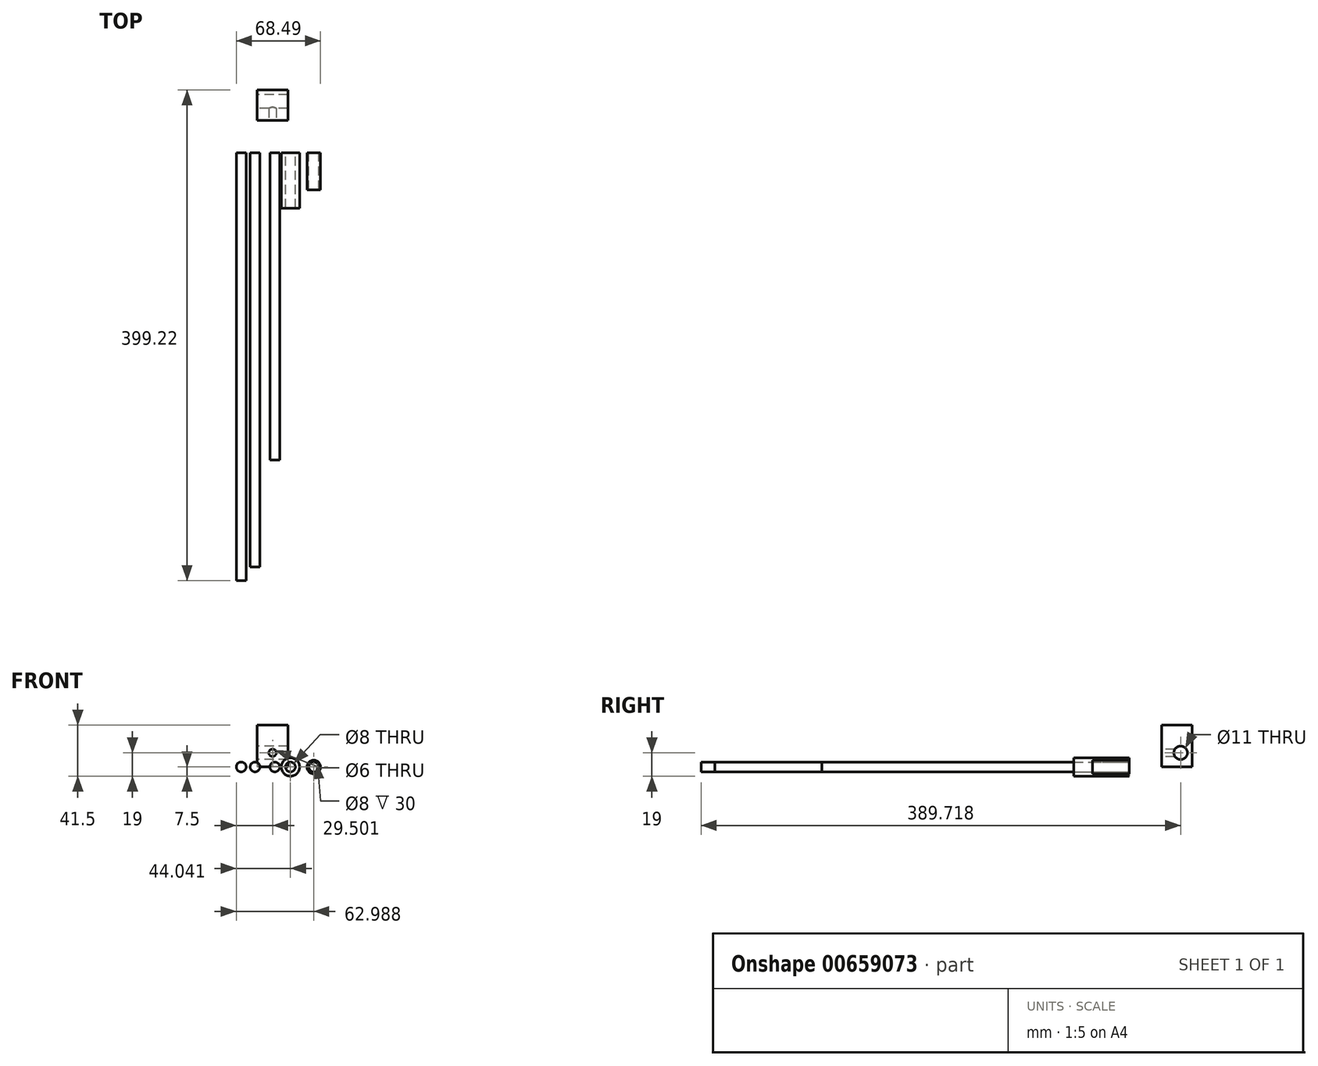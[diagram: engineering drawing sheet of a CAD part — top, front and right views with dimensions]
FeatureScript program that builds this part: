
annotation { "Feature Type Name" : "Feature", "Feature Type Description" : "" }
export const myFeature = defineFeature(function(context is Context, id is Id, definition is map)
    precondition{}
    {
        {
            var Q0;
            Q0=qCreatedBy(makeId("Front.planeOp"),FACE);
            var sketch = newSketch(context, id + "F0", { "sketchPlane" : qUnion([Q0])});
            skCircle(sketch, "E0", {"center": v(-61.9, 0) * mm, "radius": 4 * mm});
            skSolve(sketch);
        }
        {
            var Q0;
            Q0=makeQuery(id+"F0.imprint","IMPRINT",FACE,{"disambiguationData":[TD([[makeQuery(id+"F0.imprint","IMPRINT",EDGE,{"derivedFrom":sQuery(id+"F0.wireOp",EDGE,"E0")}),1.0]])]});
            extrude(context, id + "F1", {"entities" : qUnion([Q0]), "depth" : 348 * mm});
        }
        {
            var Q0;
            Q0=qCreatedBy(makeId("Front.planeOp"),FACE);
            var sketch = newSketch(context, id + "F2", { "sketchPlane" : qUnion([Q0])});
            skCircle(sketch, "E1", {"center": v(-45.77, 0) * mm, "radius": 4 * mm});
            skSolve(sketch);
        }
        {
            var Q0;
            Q0=makeQuery(id+"F2.imprint","IMPRINT",FACE,{"disambiguationData":[TD([[makeQuery(id+"F2.imprint","IMPRINT",EDGE,{"derivedFrom":sQuery(id+"F2.wireOp",EDGE,"E1")}),1.0]])]});
            extrude(context, id + "F3", {"entities" : qUnion([Q0]), "depth" : 250 * mm});
        }
        {
            var Q0;
            Q0=qCreatedBy(makeId("Front.planeOp"),FACE);
            var sketch = newSketch(context, id + "F4", { "sketchPlane" : qUnion([Q0])});
            skCircle(sketch, "E2", {"center": v(-33.08, 0) * mm, "radius": 4 * mm});
            skCircle(sketch, "E3", {"center": v(-33.08, 0) * mm, "radius": 7.5 * mm});
            skSolve(sketch);
        }
        {
            var Q0;
            Q0=makeQuery(id+"F4.imprint","IMPRINT",FACE,{"disambiguationData":[TD([[makeQuery(id+"F4.imprint","IMPRINT",EDGE,{"derivedFrom":sQuery(id+"F4.wireOp",EDGE,"E2")}),-1.0]])]});
            extrude(context, id + "F5", {"entities" : qUnion([Q0]), "depth" : 45 * mm, "offsetDistance" : 25 * mm});
        }
        {
            var Q0;
            Q0=makeQuery(id+"F1.opExtrude","SWEPT_BODY",BODY,{"disambiguationData":[OSD([sQuery(id+"F0.wireOp",EDGE,"E0")])]});
            transform(context, id + "F6", {"entities" : qUnion([Q0]), "transformType" : TransformType.TRANSLATION_3D, "dx" : -11.23 * mm, "dy" : 0 * mm, "dz" : 0 * mm, "makeCopy" : false});
        }
        {
            var Q0;
            Q0=qSketchRegion(id+"F0",true);
            extrude(context, id + "F7", {"entities" : qUnion([Q0]), "depth" : 337 * mm});
        }
        {
            var Q0;
            Q0=qCreatedBy(makeId("Front.planeOp"),FACE);
            var sketch = newSketch(context, id + "F8", { "sketchPlane" : qUnion([Q0])});
            skCircle(sketch, "E4", {"center": v(-14.13, 0) * mm, "radius": 4 * mm});
            skCircle(sketch, "E5", {"center": v(-14.13, 0) * mm, "radius": 5.5 * mm});
            skSolve(sketch);
        }
        {
            var Q0;
            Q0=makeQuery(id+"F8.imprint","IMPRINT",FACE,{"disambiguationData":[TD([[makeQuery(id+"F8.imprint","IMPRINT",EDGE,{"derivedFrom":sQuery(id+"F8.wireOp",EDGE,"E4")}),-1.0]])]});
            extrude(context, id + "F9", {"entities" : qUnion([Q0]), "depth" : 30 * mm});
        }
        {
            var Q0;
            Q0=qCreatedBy(makeId("Top.planeOp"),FACE);
            var sketch = newSketch(context, id + "F10", { "sketchPlane" : qUnion([Q0])});
            skLineSegment(sketch, "E6.bottom", {"start": v(-35.12, 51.22) * mm, "end": v(-60.12, 51.22) * mm});
            skLineSegment(sketch, "E6.top", {"start": v(-35.12, 26.22) * mm, "end": v(-60.12, 26.22) * mm});
            skLineSegment(sketch, "E6.left", {"start": v(-35.12, 51.22) * mm, "end": v(-35.12, 26.22) * mm});
            skLineSegment(sketch, "E6.right", {"start": v(-60.12, 51.22) * mm, "end": v(-60.12, 26.22) * mm});
            skSolve(sketch);
        }
        {
            var Q0;
            Q0=makeQuery(id+"F10.imprint","IMPRINT",FACE,{"disambiguationData":[TD([[makeQuery(id+"F10.imprint","IMPRINT",EDGE,{"derivedFrom":sQuery(id+"F10.wireOp",EDGE,"E6.bottom")}),1.0]])]});
            extrude(context, id + "F11", {"entities" : qUnion([Q0]), "depth" : 34 * mm});
        }
        {
            var Q0;
            Q0=makeQuery(id+"F11.opExtrude","SWEPT_FACE",FACE,{"disambiguationData":[OSD([sQuery(id+"F10.wireOp",EDGE,"E6.right")])]});
            var sketch = newSketch(context, id + "F12", { "sketchPlane" : qUnion([Q0])});
            skLineSegment(sketch, "E7", {"start": v(-32.12, 0) * mm, "end": v(-51.22, 0) * mm, "construction": true});
            skLineSegment(sketch, "E8", {"start": v(-51.22, 0) * mm, "end": v(-51.22, 22.36) * mm, "construction": true});
            skCircle(sketch, "E9", {"center": v(-41.72, 11.5) * mm, "radius": 5.5 * mm});
            skSolve(sketch);
        }
        {
            var Q0;
            Q0=makeQuery(id+"F12.imprint","IMPRINT",FACE,{"disambiguationData":[TD([[makeQuery(id+"F12.imprint","IMPRINT",EDGE,{"derivedFrom":sQuery(id+"F12.wireOp",EDGE,"E9")}),1.0]])]});
            extrude(context, id + "F13", {"entities" : qUnion([Q0]), "operationType" : NewBodyOperationType.REMOVE, "endBound" : BoundingType.THROUGH_ALL, "oppositeDirection" : true, "depth" : 25 * mm});
        }
        {
            var Q0;
            Q0=makeQuery(id+"F11.opExtrude","SWEPT_FACE",FACE,{"disambiguationData":[OSD([sQuery(id+"F10.wireOp",EDGE,"E6.top")])]});
            var sketch = newSketch(context, id + "F14", { "sketchPlane" : qUnion([Q0])});
            skLineSegment(sketch, "E10.0", {"start": v(-60.12, 6) * mm, "end": v(-60.12, 17) * mm, "construction": true});
            skLineSegment(sketch, "E11", {"start": v(-60.12, 17) * mm, "end": v(-35.12, 17) * mm, "construction": true});
            skLineSegment(sketch, "E12", {"start": v(-60.12, 6) * mm, "end": v(-35.12, 6) * mm, "construction": true});
            skLineSegment(sketch, "E13", {"start": v(-60.12, 17) * mm, "end": v(-60.12, 11.5) * mm, "construction": true});
            skLineSegment(sketch, "E14", {"start": v(-60.12, 11.5) * mm, "end": v(-35.12, 11.5) * mm, "construction": true});
            skCircle(sketch, "E15", {"center": v(-47.62, 11.5) * mm, "radius": 3 * mm});
            skSolve(sketch);
        }
        {
            var Q0;
            Q0=makeQuery(id+"F14.imprint","IMPRINT",FACE,{"disambiguationData":[TD([[makeQuery(id+"F14.imprint","IMPRINT",EDGE,{"derivedFrom":sQuery(id+"F14.wireOp",EDGE,"E15")}),1.0]])]});
            extrude(context, id + "F15", {"entities" : qUnion([Q0]), "operationType" : NewBodyOperationType.REMOVE, "endBound" : BoundingType.UP_TO_NEXT, "oppositeDirection" : true, "depth" : 25 * mm});
        }
    });
